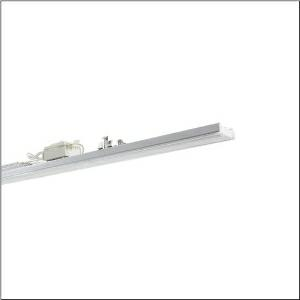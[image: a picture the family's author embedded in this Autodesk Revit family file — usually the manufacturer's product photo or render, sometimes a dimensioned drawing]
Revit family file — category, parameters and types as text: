
# Revit family: licross_11_recessed_ho_51tl18mv4hxm
name_source: partatom
category: Lighting Fixtures
units: mm (PartAtom-declared; Revit-internal decimal feet)

## family parameters
Cut with Voids When Loaded = No
Host = Face
Light Source = No
Part Type = Normal
Room Calculation Point = No
Round Connector Dimension = Use Diameter
Shared = No

## types (1)
- --- (1 x LED, 17090 lm, 89.2 W, 4000K)
    Apparent Load = 89 VA
    CIE Flux Codes = 78 94 99 100 100
    Color Rendering = 80
    Color Temperature = 4000K
    Default Elevation = 1800 mm
    Description = Licross 11 Recessed HO, luminaire insert, of sheet steel, coil coated, white, length: 2.250mm, width: 66mm, height: 67mm, LED rated luminous flux: 17.090lm, light colour: 840, SDCM (Standard Deviation of Colour Matching)MacAdam ≤ 2 SDCM (initial), control gear: ON/OFF Multilumen, with plug, 3-pole, with phase selection, mains connection: 220..240V, AC, 50/60Hz, rated input power: 89W, internal wiring halogen-free, primary light control with lens, of plastic, primary optical cover: cover, of PMMA, light emission: direct distribution, primary light characteristic: symmetric, protection rating (complete): IP40, insulation class (complete): insulation class I (protective earthing), certification: CE, ENEC, VDE, UKCA, protection symbol: D if used in an environment without relevant dust loads with corresponding accessories, impact resistance: IK06, permissible ambient temperature for indoor applications: -35..+35°C, corresponds to IFS (International Featured Standards) requirements for safety and quality in the food industry, reducing of maximum allowable ambient temperature of 5°C with ceiling mounting, The light source and the operating device comply with the requirements of the Ecodesign Regulation (EU) 2019/2020 and are replaceable in accordance with this regulation, packaging unit: 1 piece
    Height = 58 mm
    Lamp = 1 x LED
    Lamp Light Flux = 17090 lm
    Lamp Power = 89.2 W
    Lamp count = 1
    Length = 2250 mm
    Luminous efficacy = 192 lm/W
    Manufacturer = Siteco
    ModVariant = No
    Model = 51TL18MV4HXM
    Mounting Place = Ceiling
    Mounting Type = Pendant
    Number of Poles = 1
    OnlyDefault = Yes
    Power Factor = 1
    Product Name = Licross 11 Recessed HO
    Product group = luminaire insert | ceiling pendant
    ProductGroupID = 901
    Protection Class = Protection class I
    Protection Degree = IP 40
    RLX_Detail_Level = 1
    RLX_Emergency_Light_Flux = 0 lm
    RLX_Emergency_Type = 0
    RLX_Emergency_Type_DB = No
    RlxData = <blob elided: 27257 chars, md5=5046b6d4>
    Socket = socket
    Standby Power = 0 W
    System Light Flux = 17090 lm
    System Power = 89 W
    Type Comments = factory setting: luminous flux: 100 % | (A | C | E) | 210 mA
    Type Image = l_1296930.jpg
    URL = http://relux.com
    VarID = @adj_089551
    Voltage = 0 V
    Weight = 0.00 kg
    Width = 66 mm

## geometry (parser evidence)
native form markers: Blend x4, Sweep x9
no freeform markers — native parametric forms only
